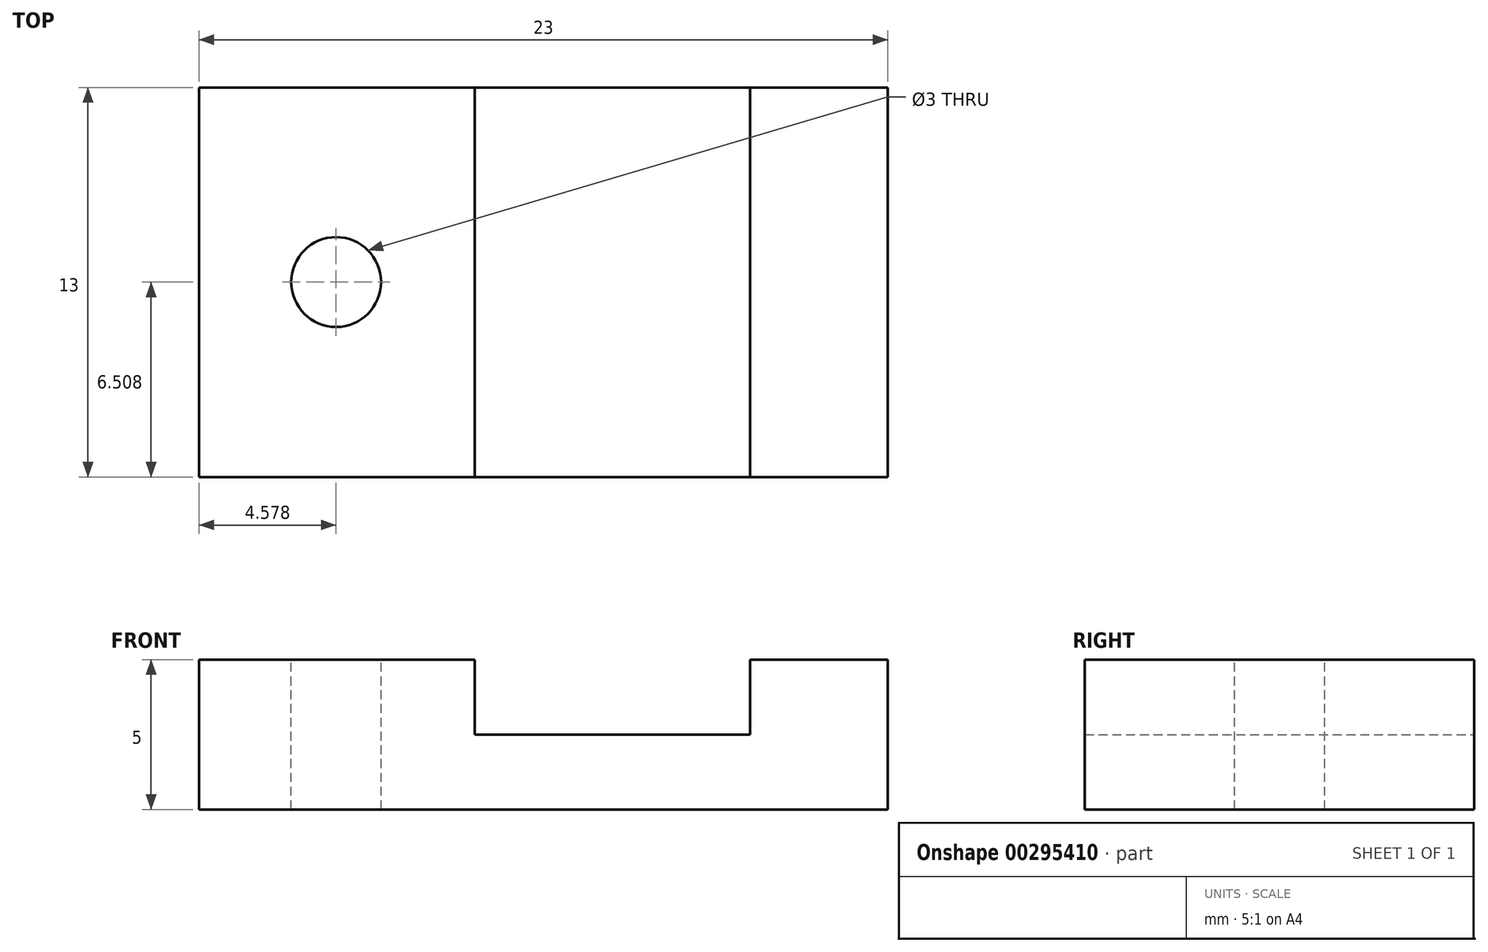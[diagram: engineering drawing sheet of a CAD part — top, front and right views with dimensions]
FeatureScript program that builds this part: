
annotation { "Feature Type Name" : "Feature", "Feature Type Description" : "" }
export const myFeature = defineFeature(function(context is Context, id is Id, definition is map)
    precondition{}
    {
        {
            var Q0;
            Q0=qCreatedBy(makeId("Front.planeOp"),FACE);
            var sketch = newSketch(context, id + "F0", { "sketchPlane" : qUnion([Q0])});
            skLineSegment(sketch, "E0", {"start": v(-54.8, 0) * mm, "end": v(-31.8, 0) * mm});
            skLineSegment(sketch, "E1", {"start": v(-54.8, 0) * mm, "end": v(-54.8, 5) * mm});
            skLineSegment(sketch, "E2", {"start": v(-31.8, 0) * mm, "end": v(-31.8, 5) * mm});
            skLineSegment(sketch, "E3", {"start": v(-54.8, 5) * mm, "end": v(-45.6, 5) * mm});
            skLineSegment(sketch, "E4", {"start": v(-45.6, 5) * mm, "end": v(-45.6, 2.5) * mm});
            skLineSegment(sketch, "E5", {"start": v(-45.6, 2.5) * mm, "end": v(-36.4, 2.5) * mm});
            skLineSegment(sketch, "E6", {"start": v(-36.4, 2.5) * mm, "end": v(-36.4, 5) * mm});
            skLineSegment(sketch, "E7", {"start": v(-36.4, 5) * mm, "end": v(-31.8, 5) * mm});
            skSolve(sketch);
        }
        {
            var Q0;
            Q0=makeQuery(id+"F0.imprint","IMPRINT",FACE,{"disambiguationData":[TD([[makeQuery(id+"F0.imprint","IMPRINT",EDGE,{"derivedFrom":sQuery(id+"F0.wireOp",EDGE,"E0")}),1.0]])]});
            extrude(context, id + "F1", {"entities" : qUnion([Q0]), "depth" : 13 * mm});
        }
        {
            var Q0;
            Q0=makeQuery(id+"F1.opExtrude","SWEPT_FACE",FACE,{"disambiguationData":[OSD([sQuery(id+"F0.wireOp",EDGE,"E3")])]});
            var sketch = newSketch(context, id + "F2", { "sketchPlane" : qUnion([Q0])});
            skLineSegment(sketch, "E8", {"start": v(-50.2, 0) * mm, "end": v(-50.2, -5) * mm});
            skLineSegment(sketch, "E9", {"start": v(-50.2, -13) * mm, "end": v(-50.2, -8) * mm});
            skPoint(sketch, "E10", {"position": v(-50.22, -6.5) * mm});
            skLineSegment(sketch, "E11", {"start": v(-54.8, -6.5) * mm, "end": v(-51.8, -6.5) * mm});
            skLineSegment(sketch, "E12", {"start": v(-45.6, -6.5) * mm, "end": v(-48.6, -6.5) * mm});
            skSolve(sketch);
        }
        {
            var Q0;
            Q0=sQuery(id+"F2.wireOp",VERTEX,"E10");
            var Q1;
            Q1=makeQuery(id+"F1.opExtrude","SWEPT_BODY",BODY,{"disambiguationData":[OSD([sQuery(id+"F0.wireOp",EDGE,"E0"),sQuery(id+"F0.wireOp",EDGE,"E1"),sQuery(id+"F0.wireOp",EDGE,"E2"),sQuery(id+"F0.wireOp",EDGE,"E3"),sQuery(id+"F0.wireOp",EDGE,"E4"),sQuery(id+"F0.wireOp",EDGE,"E5"),sQuery(id+"F0.wireOp",EDGE,"E6"),sQuery(id+"F0.wireOp",EDGE,"E7")])]});
            hole(context, id + "F3", {"style" : HoleStyle.SIMPLE, "endStyle" : HoleEndStyle.THROUGH, "holeDiameter" : 3 * mm, "tappedDepth" : 12 * mm, "tapClearance" : 3, "locations" : qUnion([Q0]), "scope" : qUnion([Q1])});
        }
    });
